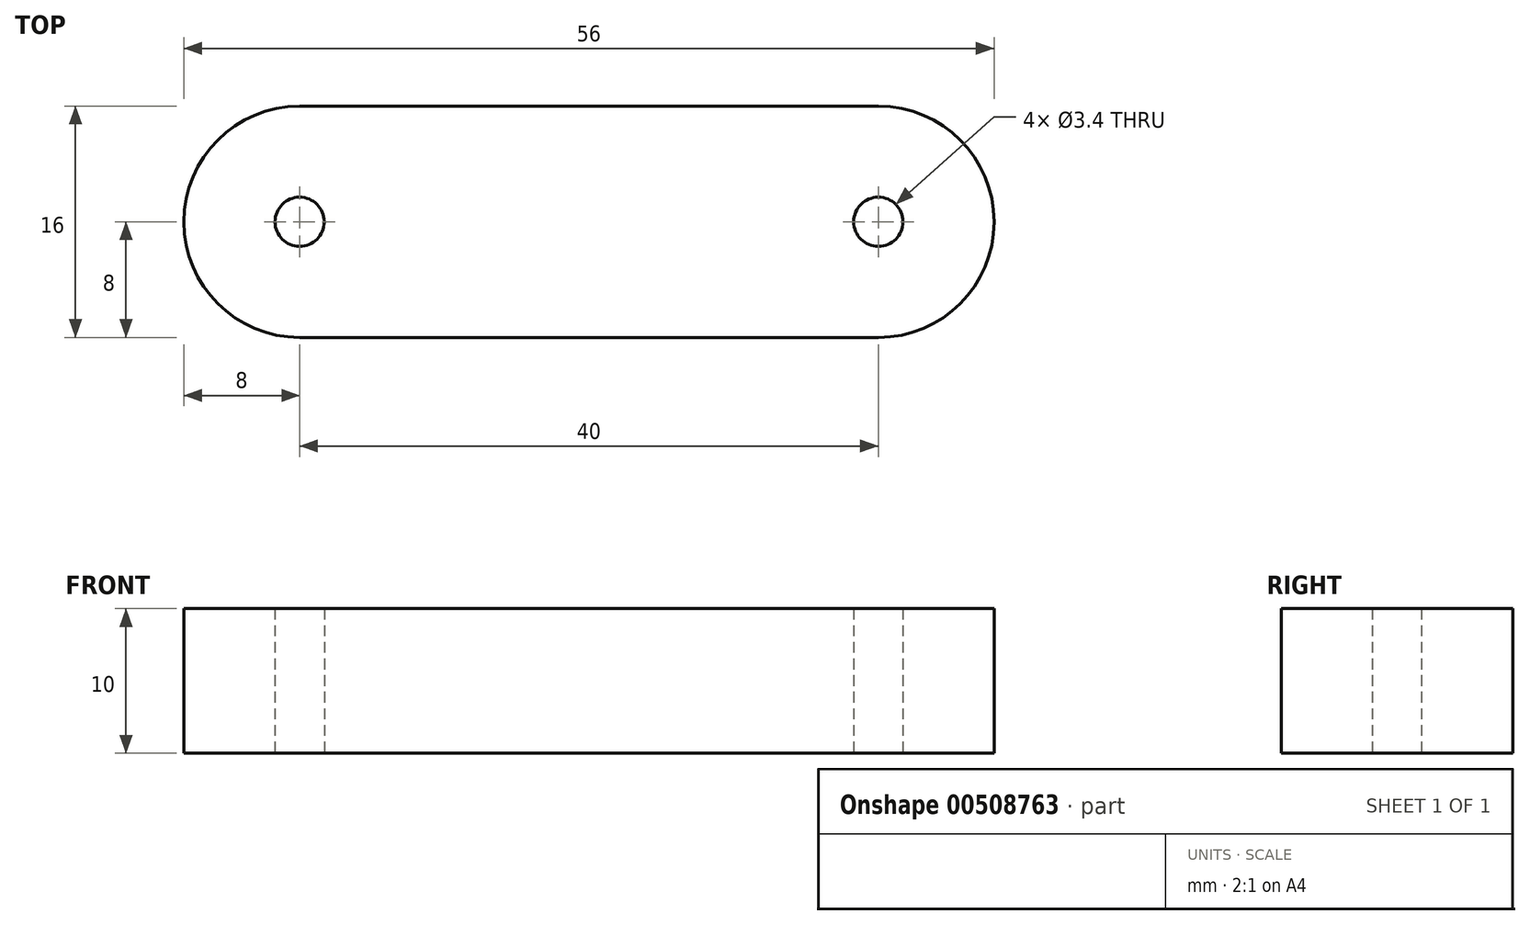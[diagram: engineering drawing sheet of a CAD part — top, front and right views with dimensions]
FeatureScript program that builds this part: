
annotation { "Feature Type Name" : "Feature", "Feature Type Description" : "" }
export const myFeature = defineFeature(function(context is Context, id is Id, definition is map)
    precondition{}
    {
        {
            var Q0;
            Q0=qCreatedBy(makeId("Top.planeOp"),FACE);
            var sketch = newSketch(context, id + "F0", { "sketchPlane" : qUnion([Q0])});
            skLineSegment(sketch, "E0.bottom", {"start": v(-20, 8) * mm, "end": v(20, 8) * mm});
            skLineSegment(sketch, "E0.top", {"start": v(-20, -8) * mm, "end": v(20, -8) * mm});
            skLineSegment(sketch, "E0.left", {"start": v(-20, 8) * mm, "end": v(-20, -8) * mm});
            skLineSegment(sketch, "E0.right", {"start": v(20, 8) * mm, "end": v(20, -8) * mm});
            skPoint(sketch, "E0.middle", {"position": v(0, 0) * mm});
            skArc(sketch, "E1", {"start": v(-20, 8) * mm, "mid": v(-28, 0) * mm, "end": v(-20, -8) * mm});
            skArc(sketch, "E2", {"start": v(20, -8) * mm, "mid": v(28, 0) * mm, "end": v(20, 8) * mm});
            skCircle(sketch, "E3", {"center": v(-20, 0) * mm, "radius": 1.7 * mm});
            skCircle(sketch, "E4", {"center": v(20, 0) * mm, "radius": 1.7 * mm});
            skSolve(sketch);
        }
        {
            var Q0;
            Q0 = qSketchRegion(id + "F0", true);
            extrude(context, id + "F1", {"entities" : qUnion([Q0]), "depth" : 10 * mm, "offsetDistance" : 25 * mm});
        }
    });
